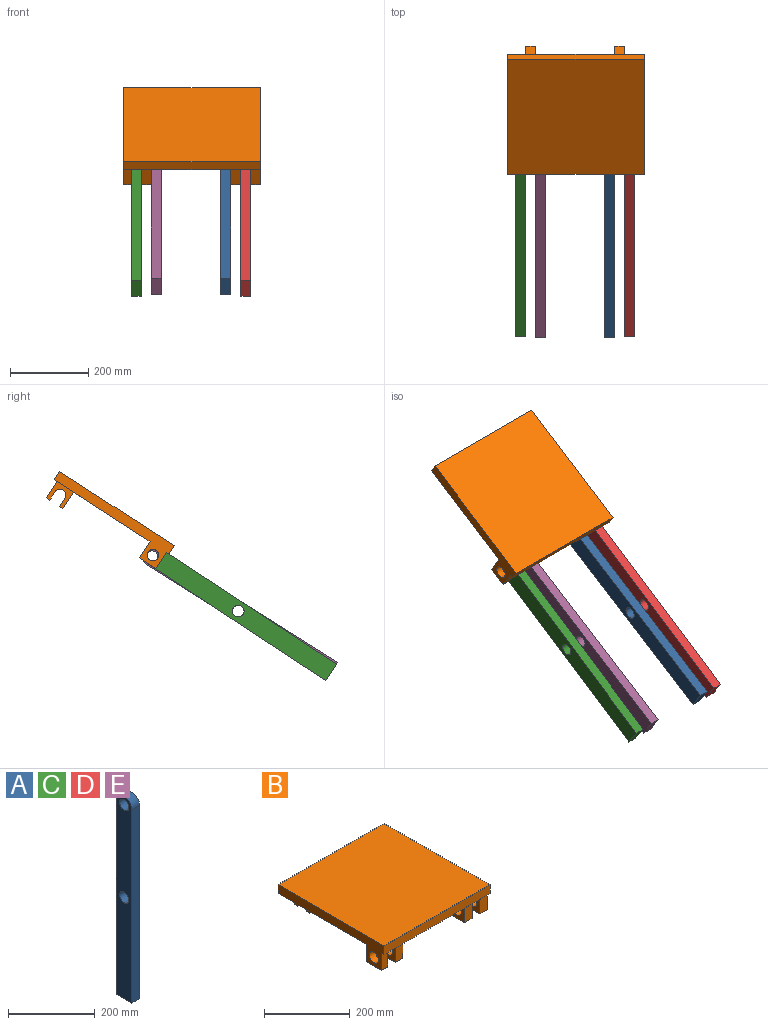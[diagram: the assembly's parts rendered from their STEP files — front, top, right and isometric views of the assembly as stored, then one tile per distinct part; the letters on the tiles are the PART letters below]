
ASSEMBLY  parts=5 mates=10
PART A: 8 faces, bbox 25x50x570 mm
  f0: plane 545x25mm, normal (0,-1,0), area 13625mm2, adj f1,f5,f6,f7
  f1: plane 50x25mm, normal (0,0,-1), area 1250mm2, adj f0,f4,f5,f6
  f2: cylinder r=15mm len=30mm, axis (-1,0,0), area 2356.2mm2, adj f5,f6
  f3: cylinder r=15mm len=30mm, axis (-1,0,0), area 2356.2mm2, adj f5,f6
  f4: plane 545x25mm, normal (0,1,0), area 13625mm2, adj f1,f5,f6,f7
  f5: plane 570x50mm, normal (1,0,0), area 26818mm2, adj f0,f1,f2,f3,f4,f7
  f6: plane 570x50mm, normal (-1,0,0), area 26818mm2, adj f0,f1,f2,f3,f4,f7
  f7: cylinder r=25mm len=50mm, axis (-1,0,0), area 1963.5mm2, adj f0,f4,f5,f6
PART B: 46 faces, bbox 350x350x75 mm
  f0: plane 25x10mm, normal (0,0,-1), area 250mm2, adj f27,f28,f29,f40
  f1: plane 25x10mm, normal (0,0,-1), area 250mm2, adj f32,f33,f34,f36
  f2: plane 350x25mm, normal (0,1,0), area 8750mm2, adj f3,f5,f6,f7
  f3: plane 350x75mm, normal (-1,0,0), area 10543.1mm2, adj f2,f4,f6,f7,f8,f9,f11,f45
  f4: plane 350x25mm, normal (0,-1,0), area 8750mm2, adj f3,f5,f6,f7
  f5: plane 350x75mm, normal (1,0,0), area 10543.1mm2, adj f2,f4,f6,f7,f12,f14,f15,f44
  f6: plane 350x350mm, normal (0,0,1), area 122500mm2, adj f2,f3,f4,f5
  f7: plane 350x350mm, normal (0,0,-1), area 115250mm2, adj f2,f3,f4,f5,f8,f9,f10,f12
  f8: plane 50x20mm, normal (0,-1,0), area 1000mm2, adj f3,f7,f10,f11
  f9: plane 50x20mm, normal (0,1,0), area 1000mm2, adj f3,f7,f10,f11
  f10: plane 50x50mm, normal (1,0,0), area 1793.1mm2, adj f7,f8,f9,f11,f45
  f11: plane 50x20mm, normal (0,0,-1), area 1000mm2, adj f3,f8,f9,f10
  f12: plane 50x25mm, normal (0,-1,0), area 1250mm2, adj f5,f7,f13,f15
  f13: plane 50x50mm, normal (-1,0,0), area 1793.1mm2, adj f7,f12,f14,f15,f44
  f14: plane 50x25mm, normal (0,1,0), area 1250mm2, adj f5,f7,f13,f15
  f15: plane 50x25mm, normal (0,0,-1), area 1250mm2, adj f5,f12,f13,f14
  f16: plane 50x25mm, normal (0,-1,0), area 1250mm2, adj f7,f17,f19,f20
  f17: plane 50x50mm, normal (-1,0,0), area 1793.1mm2, adj f7,f16,f18,f20,f43
  f18: plane 50x25mm, normal (0,1,0), area 1250mm2, adj f7,f17,f19,f20
  f19: plane 50x50mm, normal (1,0,0), area 1793.1mm2, adj f7,f16,f18,f20,f43
  f20: plane 50x25mm, normal (0,0,-1), area 1250mm2, adj f16,f17,f18,f19
  f21: plane 50x25mm, normal (0,-1,0), area 1250mm2, adj f7,f22,f24,f25
  f22: plane 50x50mm, normal (-1,0,0), area 1793.1mm2, adj f7,f21,f23,f25,f42
  f23: plane 50x25mm, normal (0,1,0), area 1250mm2, adj f7,f22,f24,f25
  f24: plane 50x50mm, normal (1,0,0), area 1793.1mm2, adj f7,f21,f23,f25,f42
  f25: plane 50x25mm, normal (0,0,-1), area 1250mm2, adj f21,f22,f23,f24
  f26: plane 50x25mm, normal (0,-1,0), area 1250mm2, adj f7,f27,f29,f30
  f27: plane 50x50mm, normal (-1,0,0), area 1396.6mm2, adj f0,f7,f26,f28,f30,f39,f40,f41
  f28: plane 50x25mm, normal (0,1,0), area 1250mm2, adj f0,f7,f27,f29
  f29: plane 50x50mm, normal (1,0,0), area 1396.6mm2, adj f0,f7,f26,f28,f30,f39,f40,f41
  f30: plane 25x10mm, normal (0,0,-1), area 250mm2, adj f26,f27,f29,f41
  f31: plane 50x25mm, normal (0,-1,0), area 1250mm2, adj f7,f32,f34,f35
  f32: plane 50x50mm, normal (-1,0,0), area 1396.6mm2, adj f1,f7,f31,f33,f35,f36,f37,f38
  f33: plane 50x25mm, normal (0,1,0), area 1250mm2, adj f1,f7,f32,f34
  f34: plane 50x50mm, normal (1,0,0), area 1396.6mm2, adj f1,f7,f31,f33,f35,f36,f37,f38
  f35: plane 25x10mm, normal (0,0,-1), area 250mm2, adj f31,f32,f34,f37
  f36: plane 25x25mm, normal (0,-1,0), area 625mm2, adj f1,f32,f34,f38
  f37: plane 25x25mm, normal (0,1,0), area 625mm2, adj f32,f34,f35,f38
  f38: cylinder r=15mm len=30mm, axis (-1,0,0), area 1178.1mm2, adj f32,f34,f36,f37
  f39: cylinder r=15mm len=30mm, axis (-1,0,0), area 1178.1mm2, adj f27,f29,f40,f41
  f40: plane 25x25mm, normal (0,-1,0), area 625mm2, adj f0,f27,f29,f39
  f41: plane 25x25mm, normal (0,1,0), area 625mm2, adj f27,f29,f30,f39
  f42: cylinder r=15mm len=30mm, axis (1,0,0), area 2356.2mm2, adj f22,f24
  f43: cylinder r=15mm len=30mm, axis (1,0,0), area 2356.2mm2, adj f17,f19
  f44: cylinder r=15mm len=30mm, axis (1,0,0), area 2356.2mm2, adj f5,f13
  f45: cylinder r=15mm len=30mm, axis (1,0,0), area 1885mm2, adj f3,f10
PART C: same geometry as A
PART D: same geometry as A
PART E: same geometry as A
PLACE A rot(axis=(-1,0,0),57.7deg) t=(-32.34,117.59,185.7)mm
PLACE B rot(axis=(1,0,0),32.8deg) t=(-216.19,185.83,326.2)mm
PLACE C rot(axis=(-1,0,0),56.7deg) t=(-261.34,116.78,188.72)mm
PLACE D rot(axis=(-1,0,0),56.7deg) t=(18.66,116.78,188.72)mm
PLACE E rot(axis=(-1,0,0),57.7deg) t=(-210.34,117.59,185.7)mm
MATE cylindrical C.f2 <-> B.f42  axis (1,0,0) through (-236.34,170.28,286.4)mm
MATE planar C.f2 <-> B.f42  axis (-1,0,0) through (-261.34,170.28,286.4)mm
MATE cylindrical E.f2 <-> A.f2  axis (-1,0,0) through (-197.84,172.87,282.37)mm
MATE cylindrical C.f3 <-> D.f3  axis (-1,0,0) through (-261.34,-47.8,143)mm
MATE planar A.f5 <-> B.f32  axis (1,0,0) through (-7.34,-55.98,137.84)mm
MATE planar D.f2 <-> B.f42  axis (1,0,0) through (43.66,170.28,286.4)mm
MATE cylindrical D.f2 <-> C.f2  axis (1,0,0) through (43.66,170.28,286.4)mm
MATE cylindrical D.f3 <-> A.f3  axis (1,0,0) through (43.66,-47.8,143)mm
MATE cylindrical E.f3 <-> C.f3  axis (1,0,0) through (-185.34,-47.8,143)mm
MATE planar E.f6 <-> B.f29  axis (-1,0,0) through (-210.34,-55.98,137.84)mm
